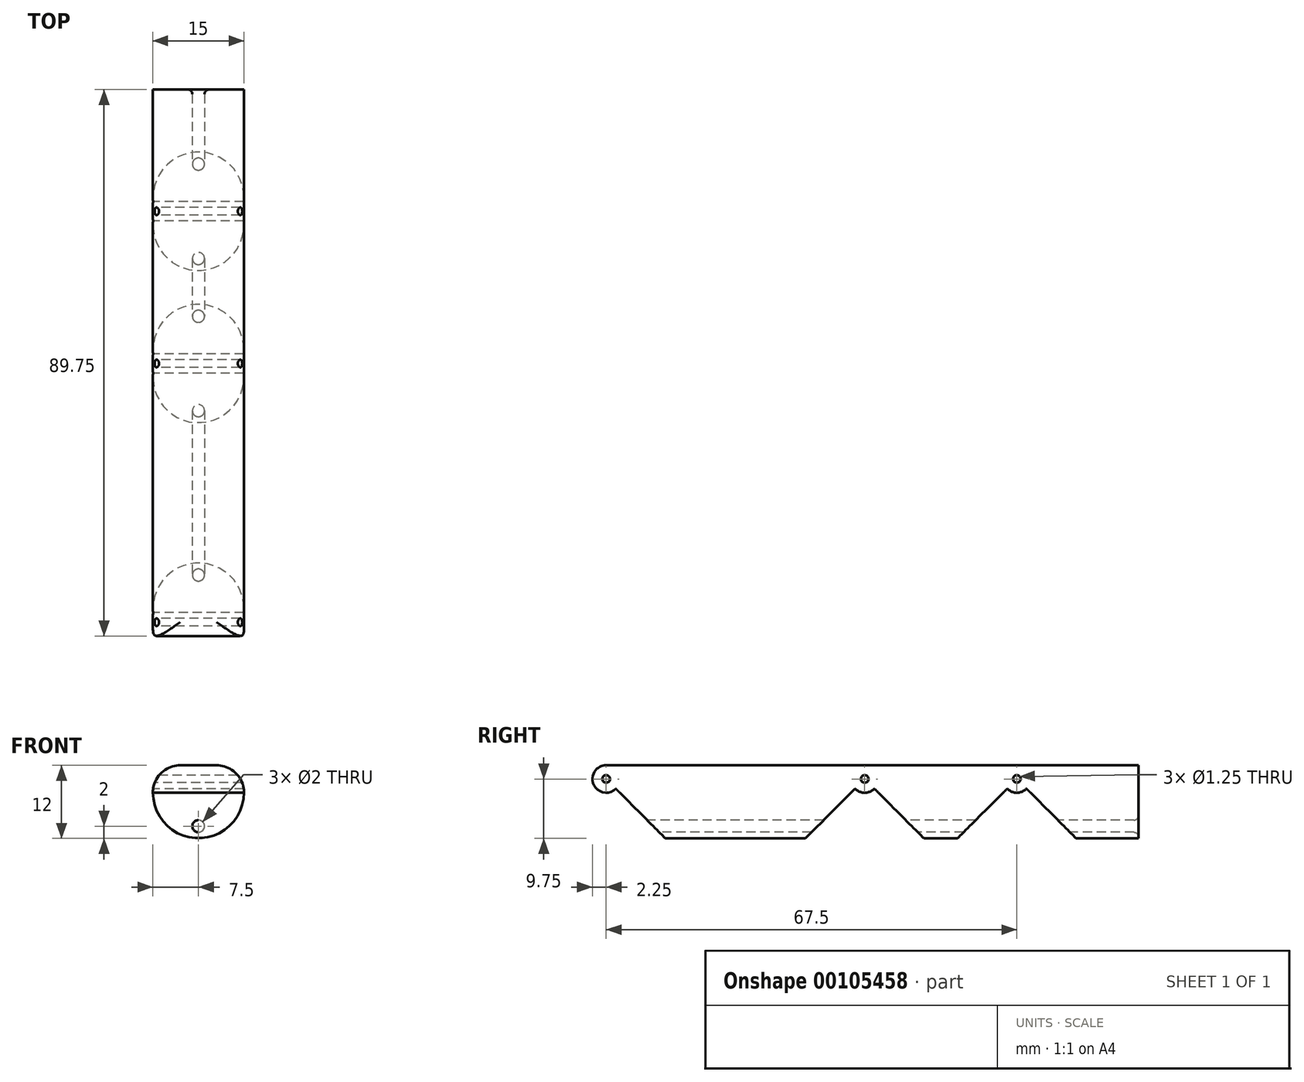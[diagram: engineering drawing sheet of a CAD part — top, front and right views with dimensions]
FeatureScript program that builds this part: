
annotation { "Feature Type Name" : "Feature", "Feature Type Description" : "" }
export const myFeature = defineFeature(function(context is Context, id is Id, definition is map)
    precondition{}
    {
        {
            assignVariable(context, id + "F0", {"name" : "FingerL1", "anyValue" : 42.5 * mm});
        }
        {
            assignVariable(context, id + "F1", {"name" : "FingerL2", "anyValue" : 25 * mm});
        }
        {
            assignVariable(context, id + "F2", {"name" : "FingerL3", "anyValue" : 20 * mm});
        }
        {
            assignVariable(context, id + "F3", {"name" : "FingerW", "anyValue" : 15 * mm});
        }
        {
            assignVariable(context, id + "F4", {"variableType" : VariableType.LENGTH, "name" : "FingerH", "lengthValue" : 12 * mm});
        }
        {
            var Q0;
            Q0=qCreatedBy(makeId("Front.planeOp"),FACE);
            var sketch = newSketch(context, id + "F5", { "sketchPlane" : qUnion([Q0])});
            skArc(sketch, "E0", {"start": v(-7.5, 0) * mm, "mid": v(0, -7.5) * mm, "end": v(7.5, 0) * mm});
            skArc(sketch, "E1", {"start": v(-7.5, 0) * mm, "mid": v(-6.18, 3.18) * mm, "end": v(-3, 4.5) * mm});
            skArc(sketch, "E2", {"start": v(7.5, 0) * mm, "mid": v(6.18, 3.18) * mm, "end": v(3, 4.5) * mm});
            skLineSegment(sketch, "E3", {"start": v(-3, 4.5) * mm, "end": v(3, 4.5) * mm});
            skCircle(sketch, "E4", {"center": v(0, -5.5) * mm, "radius": 1 * mm});
            skSolve(sketch);
        }
        {
            var Q0;
            Q0 = qSketchRegion(id + "F5", true);
            extrude(context, id + "F6", {"entities" : qUnion([Q0]), "oppositeDirection" : true, "depth" : getVariable(context, 'FingerL1') + getVariable(context, 'FingerL2') + getVariable(context, 'FingerL3'), "offsetDistance" : 25 * mm, "hasSecondDirection" : true, "secondDirectionOppositeDirection" : false, "secondDirectionDepth" : (getVariable(context, 'FingerH') - getVariable(context, 'FingerW') / 2) / 2});
        }
        {
            var Q0;
            Q0=qCreatedBy(makeId("Right.planeOp"),FACE);
            var sketch = newSketch(context, id + "F7", { "sketchPlane" : qUnion([Q0])});
            skLineSegment(sketch, "E5", {"start": v(0, 2.25) * mm, "end": v(42.5, 2.25) * mm});
            skLineSegment(sketch, "E6", {"start": v(42.5, 2.25) * mm, "end": v(67.5, 2.25) * mm});
            skLineSegment(sketch, "E7", {"start": v(67.5, 2.25) * mm, "end": v(87.5, 2.25) * mm});
            skCircle(sketch, "E8", {"center": v(42.5, 2.25) * mm, "radius": 0.63 * mm});
            skCircle(sketch, "E9", {"center": v(67.5, 2.25) * mm, "radius": 0.62 * mm});
            skCircle(sketch, "E10", {"center": v(42.5, 2.25) * mm, "radius": 2.25 * mm});
            skCircle(sketch, "E11", {"center": v(67.5, 2.25) * mm, "radius": 2.25 * mm});
            skCircle(sketch, "E12", {"center": v(0, 2.25) * mm, "radius": 0.63 * mm});
            skCircle(sketch, "E13", {"center": v(0, 2.25) * mm, "radius": 2.25 * mm});
            skLineSegment(sketch, "E14", {"start": v(0, 2.25) * mm, "end": v(9.75, -7.5) * mm});
            skLineSegment(sketch, "E15", {"start": v(9.75, -7.5) * mm, "end": v(32.75, -7.5) * mm});
            skLineSegment(sketch, "E16", {"start": v(32.75, -7.5) * mm, "end": v(42.5, 2.25) * mm});
            skLineSegment(sketch, "E17", {"start": v(42.5, 2.25) * mm, "end": v(52.25, -7.5) * mm});
            skLineSegment(sketch, "E18", {"start": v(52.25, -7.5) * mm, "end": v(57.75, -7.5) * mm});
            skLineSegment(sketch, "E19", {"start": v(57.75, -7.5) * mm, "end": v(67.5, 2.25) * mm});
            skLineSegment(sketch, "E20", {"start": v(67.5, 2.25) * mm, "end": v(77.25, -7.5) * mm});
            skLineSegment(sketch, "E21", {"start": v(77.25, -7.5) * mm, "end": v(87.5, -7.5) * mm});
            skLineSegment(sketch, "E22", {"start": v(87.5, -7.5) * mm, "end": v(87.5, 2.25) * mm});
            skPoint(sketch, "E23.0", {"position": v(0, -7.5) * mm});
            skCircle(sketch, "E24", {"center": v(0, 2.25) * mm, "radius": 3 * mm});
            skCircle(sketch, "E25", {"center": v(42.5, 2.25) * mm, "radius": 3 * mm});
            skCircle(sketch, "E26", {"center": v(67.5, 2.25) * mm, "radius": 3 * mm});
            skPoint(sketch, "E27.0", {"position": v(87.5, 4.5) * mm});
            skLineSegment(sketch, "E28", {"start": v(87.5, 2.25) * mm, "end": v(87.5, 4.5) * mm});
            skLineSegment(sketch, "E29", {"start": v(87.5, 4.5) * mm, "end": v(0, 4.5) * mm});
            skSolve(sketch);
        }
        {
            var Q0;
            {var subQ0=sQuery(id+"F7.wireOp",EDGE,"E13");var subQ1=sQuery(id+"F7.wireOp",EDGE,"E5");var subQ2=makeQuery(id+"F7.imprint","INTERSECT",VERTEX,{"derivedFrom":[subQ1,subQ0]});Q0=makeQuery(id+"F7.imprint","IMPRINT",FACE,{"disambiguationData":[TD([[makeQuery(id+"F7.imprint","IMPRINT",EDGE,{"disambiguationData":[TD([[subQ2,1.0]])],"derivedFrom":subQ1}),1.0]])]});}
            var Q1;
            {var subQ0=sQuery(id+"F7.wireOp",EDGE,"E13");var subQ1=sQuery(id+"F7.wireOp",EDGE,"E5");var subQ2=makeQuery(id+"F7.imprint","INTERSECT",VERTEX,{"derivedFrom":[subQ1,subQ0]});Q1=makeQuery(id+"F7.imprint","IMPRINT",FACE,{"disambiguationData":[TD([[makeQuery(id+"F7.imprint","IMPRINT",EDGE,{"disambiguationData":[TD([[subQ2,1.0]])],"derivedFrom":subQ1}),-1.0]])]});}
            var Q2;
            {var subQ0=sQuery(id+"F7.wireOp",EDGE,"E24");var subQ1=sQuery(id+"F7.wireOp",EDGE,"E5");var subQ2=makeQuery(id+"F7.imprint","INTERSECT",VERTEX,{"derivedFrom":[subQ1,subQ0]});Q2=makeQuery(id+"F7.imprint","IMPRINT",FACE,{"disambiguationData":[TD([[makeQuery(id+"F7.imprint","IMPRINT",EDGE,{"disambiguationData":[TD([[subQ2,1.0]])],"derivedFrom":subQ1}),-1.0]])]});}
            var Q3;
            {var subQ0=sQuery(id+"F7.wireOp",EDGE,"E15");Q3=makeQuery(id+"F7.imprint","IMPRINT",FACE,{"disambiguationData":[TD([[makeQuery(id+"F7.imprint","IMPRINT",EDGE,{"derivedFrom":subQ0}),1.0]])]});}
            var Q4;
            {var subQ0=sQuery(id+"F7.wireOp",EDGE,"E25");var subQ1=sQuery(id+"F7.wireOp",EDGE,"E5");var subQ2=makeQuery(id+"F7.imprint","INTERSECT",VERTEX,{"derivedFrom":[subQ1,subQ0]});Q4=makeQuery(id+"F7.imprint","IMPRINT",FACE,{"disambiguationData":[TD([[makeQuery(id+"F7.imprint","IMPRINT",EDGE,{"disambiguationData":[TD([[subQ2,-1.0]])],"derivedFrom":subQ1}),-1.0]])]});}
            var Q5;
            {var subQ0=sQuery(id+"F7.wireOp",EDGE,"E10");var subQ1=sQuery(id+"F7.wireOp",EDGE,"E5");var subQ2=makeQuery(id+"F7.imprint","INTERSECT",VERTEX,{"derivedFrom":[subQ1,subQ0]});Q5=makeQuery(id+"F7.imprint","IMPRINT",FACE,{"disambiguationData":[TD([[makeQuery(id+"F7.imprint","IMPRINT",EDGE,{"disambiguationData":[TD([[subQ2,-1.0]])],"derivedFrom":subQ1}),-1.0]])]});}
            var Q6;
            {var subQ0=sQuery(id+"F7.wireOp",EDGE,"E8");var subQ1=sQuery(id+"F7.wireOp",EDGE,"E6");var subQ2=makeQuery(id+"F7.imprint","INTERSECT",VERTEX,{"derivedFrom":[subQ1,subQ0]});Q6=makeQuery(id+"F7.imprint","IMPRINT",FACE,{"disambiguationData":[TD([[makeQuery(id+"F7.imprint","IMPRINT",EDGE,{"disambiguationData":[TD([[subQ2,-1.0]])],"derivedFrom":subQ1}),-1.0]])]});}
            var Q7;
            {var subQ0=sQuery(id+"F7.wireOp",EDGE,"E25");var subQ1=sQuery(id+"F7.wireOp",EDGE,"E6");var subQ2=makeQuery(id+"F7.imprint","INTERSECT",VERTEX,{"derivedFrom":[subQ1,subQ0]});Q7=makeQuery(id+"F7.imprint","IMPRINT",FACE,{"disambiguationData":[TD([[makeQuery(id+"F7.imprint","IMPRINT",EDGE,{"disambiguationData":[TD([[subQ2,1.0]])],"derivedFrom":subQ1}),-1.0]])]});}
            var Q8;
            {var subQ0=sQuery(id+"F7.wireOp",EDGE,"E18");Q8=makeQuery(id+"F7.imprint","IMPRINT",FACE,{"disambiguationData":[TD([[makeQuery(id+"F7.imprint","IMPRINT",EDGE,{"derivedFrom":subQ0}),1.0]])]});}
            var Q9;
            {var subQ0=sQuery(id+"F7.wireOp",EDGE,"E26");var subQ1=sQuery(id+"F7.wireOp",EDGE,"E6");var subQ2=makeQuery(id+"F7.imprint","INTERSECT",VERTEX,{"derivedFrom":[subQ1,subQ0]});Q9=makeQuery(id+"F7.imprint","IMPRINT",FACE,{"disambiguationData":[TD([[makeQuery(id+"F7.imprint","IMPRINT",EDGE,{"disambiguationData":[TD([[subQ2,-1.0]])],"derivedFrom":subQ1}),-1.0]])]});}
            var Q10;
            {var subQ0=sQuery(id+"F7.wireOp",EDGE,"E11");var subQ1=sQuery(id+"F7.wireOp",EDGE,"E6");var subQ2=makeQuery(id+"F7.imprint","INTERSECT",VERTEX,{"derivedFrom":[subQ1,subQ0]});Q10=makeQuery(id+"F7.imprint","IMPRINT",FACE,{"disambiguationData":[TD([[makeQuery(id+"F7.imprint","IMPRINT",EDGE,{"disambiguationData":[TD([[subQ2,-1.0]])],"derivedFrom":subQ1}),-1.0]])]});}
            var Q11;
            {var subQ0=sQuery(id+"F7.wireOp",EDGE,"E9");var subQ1=sQuery(id+"F7.wireOp",EDGE,"E7");var subQ2=makeQuery(id+"F7.imprint","INTERSECT",VERTEX,{"derivedFrom":[subQ1,subQ0]});Q11=makeQuery(id+"F7.imprint","IMPRINT",FACE,{"disambiguationData":[TD([[makeQuery(id+"F7.imprint","IMPRINT",EDGE,{"disambiguationData":[TD([[subQ2,-1.0]])],"derivedFrom":subQ1}),-1.0]])]});}
            var Q12;
            {var subQ0=sQuery(id+"F7.wireOp",EDGE,"E26");var subQ1=sQuery(id+"F7.wireOp",EDGE,"E7");var subQ2=makeQuery(id+"F7.imprint","INTERSECT",VERTEX,{"derivedFrom":[subQ1,subQ0]});Q12=makeQuery(id+"F7.imprint","IMPRINT",FACE,{"disambiguationData":[TD([[makeQuery(id+"F7.imprint","IMPRINT",EDGE,{"disambiguationData":[TD([[subQ2,1.0]])],"derivedFrom":subQ1}),-1.0]])]});}
            var Q13;
            {var subQ0=sQuery(id+"F7.wireOp",EDGE,"E21");Q13=makeQuery(id+"F7.imprint","IMPRINT",FACE,{"disambiguationData":[TD([[makeQuery(id+"F7.imprint","IMPRINT",EDGE,{"derivedFrom":subQ0}),1.0]])]});}
            var Q14;
            {var subQ0=sQuery(id+"F7.wireOp",EDGE,"E20");var subQ1=sQuery(id+"F7.wireOp",EDGE,"E9");var subQ2=makeQuery(id+"F7.imprint","INTERSECT",VERTEX,{"derivedFrom":[subQ1,subQ0]});Q14=makeQuery(id+"F7.imprint","IMPRINT",FACE,{"disambiguationData":[TD([[makeQuery(id+"F7.imprint","IMPRINT",EDGE,{"disambiguationData":[TD([[subQ2,1.0]])],"derivedFrom":subQ1}),-1.0]])]});}
            var Q15;
            {var subQ0=sQuery(id+"F7.wireOp",EDGE,"E11");var subQ1=sQuery(id+"F7.wireOp",EDGE,"E6");var subQ2=makeQuery(id+"F7.imprint","INTERSECT",VERTEX,{"derivedFrom":[subQ1,subQ0]});Q15=makeQuery(id+"F7.imprint","IMPRINT",FACE,{"disambiguationData":[TD([[makeQuery(id+"F7.imprint","IMPRINT",EDGE,{"disambiguationData":[TD([[subQ2,-1.0]])],"derivedFrom":subQ1}),1.0]])]});}
            var Q16;
            {var subQ0=sQuery(id+"F7.wireOp",EDGE,"E17");var subQ1=sQuery(id+"F7.wireOp",EDGE,"E8");var subQ2=makeQuery(id+"F7.imprint","INTERSECT",VERTEX,{"derivedFrom":[subQ1,subQ0]});Q16=makeQuery(id+"F7.imprint","IMPRINT",FACE,{"disambiguationData":[TD([[makeQuery(id+"F7.imprint","IMPRINT",EDGE,{"disambiguationData":[TD([[subQ2,1.0]])],"derivedFrom":subQ1}),-1.0]])]});}
            var Q17;
            {var subQ0=sQuery(id+"F7.wireOp",EDGE,"E10");var subQ1=sQuery(id+"F7.wireOp",EDGE,"E5");var subQ2=makeQuery(id+"F7.imprint","INTERSECT",VERTEX,{"derivedFrom":[subQ1,subQ0]});Q17=makeQuery(id+"F7.imprint","IMPRINT",FACE,{"disambiguationData":[TD([[makeQuery(id+"F7.imprint","IMPRINT",EDGE,{"disambiguationData":[TD([[subQ2,-1.0]])],"derivedFrom":subQ1}),1.0]])]});}
            var Q18;
            {var subQ0=sQuery(id+"F7.wireOp",EDGE,"E24");var subQ1=sQuery(id+"F7.wireOp",EDGE,"E5");var subQ2=makeQuery(id+"F7.imprint","INTERSECT",VERTEX,{"derivedFrom":[subQ1,subQ0]});Q18=makeQuery(id+"F7.imprint","IMPRINT",FACE,{"disambiguationData":[TD([[makeQuery(id+"F7.imprint","IMPRINT",EDGE,{"disambiguationData":[TD([[subQ2,1.0]])],"derivedFrom":subQ1}),1.0]])]});}
            var Q19;
            {var subQ0=sQuery(id+"F7.wireOp",EDGE,"E24");var subQ1=sQuery(id+"F7.wireOp",EDGE,"E5");var subQ2=makeQuery(id+"F7.imprint","INTERSECT",VERTEX,{"derivedFrom":[subQ1,subQ0]});Q19=makeQuery(id+"F7.imprint","IMPRINT",FACE,{"disambiguationData":[TD([[makeQuery(id+"F7.imprint","IMPRINT",EDGE,{"disambiguationData":[TD([[subQ2,-1.0]])],"derivedFrom":subQ1}),1.0]])]});}
            var Q20;
            {var subQ0=sQuery(id+"F7.wireOp",EDGE,"E25");var subQ1=sQuery(id+"F7.wireOp",EDGE,"E6");var subQ2=makeQuery(id+"F7.imprint","INTERSECT",VERTEX,{"derivedFrom":[subQ1,subQ0]});Q20=makeQuery(id+"F7.imprint","IMPRINT",FACE,{"disambiguationData":[TD([[makeQuery(id+"F7.imprint","IMPRINT",EDGE,{"disambiguationData":[TD([[subQ2,1.0]])],"derivedFrom":subQ1}),1.0]])]});}
            var Q21;
            {var subQ0=sQuery(id+"F7.wireOp",EDGE,"E25");var subQ1=sQuery(id+"F7.wireOp",EDGE,"E5");var subQ2=makeQuery(id+"F7.imprint","INTERSECT",VERTEX,{"derivedFrom":[subQ1,subQ0]});Q21=makeQuery(id+"F7.imprint","IMPRINT",FACE,{"disambiguationData":[TD([[makeQuery(id+"F7.imprint","IMPRINT",EDGE,{"disambiguationData":[TD([[subQ2,-1.0]])],"derivedFrom":subQ1}),1.0]])]});}
            var Q22;
            {var subQ0=sQuery(id+"F7.wireOp",EDGE,"E25");var subQ1=sQuery(id+"F7.wireOp",EDGE,"E6");var subQ2=makeQuery(id+"F7.imprint","INTERSECT",VERTEX,{"derivedFrom":[subQ1,subQ0]});Q22=makeQuery(id+"F7.imprint","IMPRINT",FACE,{"disambiguationData":[TD([[makeQuery(id+"F7.imprint","IMPRINT",EDGE,{"disambiguationData":[TD([[subQ2,-1.0]])],"derivedFrom":subQ1}),1.0]])]});}
            var Q23;
            {var subQ0=sQuery(id+"F7.wireOp",EDGE,"E26");var subQ1=sQuery(id+"F7.wireOp",EDGE,"E6");var subQ2=makeQuery(id+"F7.imprint","INTERSECT",VERTEX,{"derivedFrom":[subQ1,subQ0]});Q23=makeQuery(id+"F7.imprint","IMPRINT",FACE,{"disambiguationData":[TD([[makeQuery(id+"F7.imprint","IMPRINT",EDGE,{"disambiguationData":[TD([[subQ2,-1.0]])],"derivedFrom":subQ1}),1.0]])]});}
            var Q24;
            {var subQ0=sQuery(id+"F7.wireOp",EDGE,"E26");var subQ1=sQuery(id+"F7.wireOp",EDGE,"E7");var subQ2=makeQuery(id+"F7.imprint","INTERSECT",VERTEX,{"derivedFrom":[subQ1,subQ0]});Q24=makeQuery(id+"F7.imprint","IMPRINT",FACE,{"disambiguationData":[TD([[makeQuery(id+"F7.imprint","IMPRINT",EDGE,{"disambiguationData":[TD([[subQ2,1.0]])],"derivedFrom":subQ1}),1.0]])]});}
            var Q25;
            {var subQ3=sQuery(id+"F7.wireOp",EDGE,"E28");Q25=makeQuery(id+"F7.imprint","IMPRINT",FACE,{"disambiguationData":[TD([[makeQuery(id+"F7.imprint","IMPRINT",EDGE,{"derivedFrom":subQ3}),1.0]])]});}
            extrude(context, id + "F8", {"entities" : qUnion([Q0, Q1, Q2, Q3, Q4, Q5, Q6, Q7, Q8, Q9, Q10, Q11, Q12, Q13, Q14, Q15, Q16, Q17, Q18, Q19, Q20, Q21, Q22, Q23, Q24, Q25]), "operationType" : NewBodyOperationType.INTERSECT, "endBound" : BoundingType.THROUGH_ALL, "depth" : 25 * mm, "offsetDistance" : 25 * mm, "hasSecondDirection" : true, "secondDirectionBound" : SecondDirectionBoundingType.THROUGH_ALL, "secondDirectionOppositeDirection" : true, "secondDirectionDepth" : 25 * mm});
        }
        {
            var Q0;
            Q0=makeQuery(id+"F8.boolean.opBoolean","INTERSECT",EDGE,{"derivedFrom":[makeQuery(id+"F6.opExtrude","SWEPT_FACE",FACE,{"disambiguationData":[OSD([sQuery(id+"F5.wireOp",EDGE,"E4")])]}),makeQuery(id+"F8.boolean.toolComplement.opBoolean","COPY",FACE,{"derivedFrom":makeQuery(id+"F8.opExtrude","SWEPT_FACE",FACE,{"disambiguationData":[OSD([sQuery(id+"F7.wireOp",EDGE,"E20")])]})})]});
            var Q1;
            Q1=makeQuery(id+"F8.boolean.opBoolean","INTERSECT",EDGE,{"derivedFrom":[makeQuery(id+"F6.opExtrude","SWEPT_FACE",FACE,{"disambiguationData":[OSD([sQuery(id+"F5.wireOp",EDGE,"E4")])]}),makeQuery(id+"F8.boolean.toolComplement.opBoolean","COPY",FACE,{"derivedFrom":makeQuery(id+"F8.opExtrude","SWEPT_FACE",FACE,{"disambiguationData":[OSD([sQuery(id+"F7.wireOp",EDGE,"E19")])]})})]});
            var Q2;
            Q2=makeQuery(id+"F8.boolean.opBoolean","INTERSECT",EDGE,{"derivedFrom":[makeQuery(id+"F6.opExtrude","SWEPT_FACE",FACE,{"disambiguationData":[OSD([sQuery(id+"F5.wireOp",EDGE,"E4")])]}),makeQuery(id+"F8.boolean.toolComplement.opBoolean","COPY",FACE,{"derivedFrom":makeQuery(id+"F8.opExtrude","SWEPT_FACE",FACE,{"disambiguationData":[OSD([sQuery(id+"F7.wireOp",EDGE,"E17")])]})})]});
            var Q3;
            Q3=makeQuery(id+"F8.boolean.opBoolean","INTERSECT",EDGE,{"derivedFrom":[makeQuery(id+"F6.opExtrude","SWEPT_FACE",FACE,{"disambiguationData":[OSD([sQuery(id+"F5.wireOp",EDGE,"E4")])]}),makeQuery(id+"F8.boolean.toolComplement.opBoolean","COPY",FACE,{"derivedFrom":makeQuery(id+"F8.opExtrude","SWEPT_FACE",FACE,{"disambiguationData":[OSD([sQuery(id+"F7.wireOp",EDGE,"E16")])]})})]});
            var Q4;
            Q4=makeQuery(id+"F8.boolean.opBoolean","INTERSECT",EDGE,{"derivedFrom":[makeQuery(id+"F6.opExtrude","SWEPT_FACE",FACE,{"disambiguationData":[OSD([sQuery(id+"F5.wireOp",EDGE,"E4")])]}),makeQuery(id+"F8.boolean.toolComplement.opBoolean","COPY",FACE,{"derivedFrom":makeQuery(id+"F8.opExtrude","SWEPT_FACE",FACE,{"disambiguationData":[OSD([sQuery(id+"F7.wireOp",EDGE,"E14")])]})})]});
            var Q5;
            Q5=makeQuery(id+"F6.opExtrude","CAP_EDGE",EDGE,{"disambiguationData":[OSD([sQuery(id+"F5.wireOp",EDGE,"E4")])],"isStart":false});
            fillet(context, id + "F9", {"entities" : qUnion([Q0, Q1, Q2, Q3, Q4, Q5]), "tangentPropagation" : true, "radius" : 0.75 * mm, "defaultsChanged" : true, "vertexSettings" : [], "allowEdgeOverflow" : false});
        }
    });
